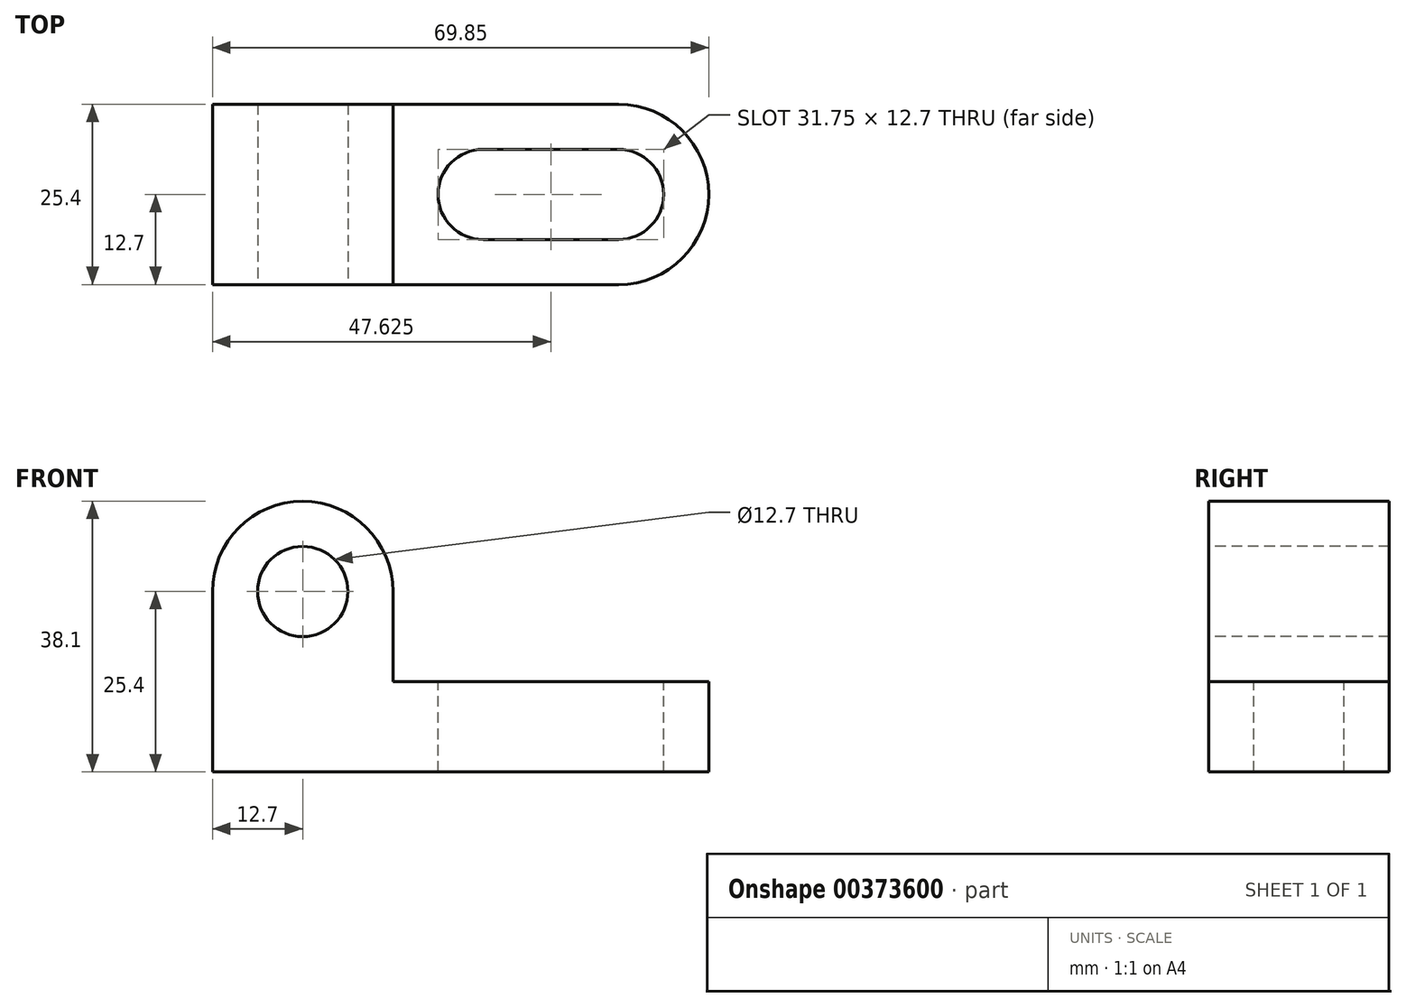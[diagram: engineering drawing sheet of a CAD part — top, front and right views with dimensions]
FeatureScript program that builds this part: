
annotation { "Feature Type Name" : "Feature", "Feature Type Description" : "" }
export const myFeature = defineFeature(function(context is Context, id is Id, definition is map)
    precondition{}
    {
        {
            var Q0;
            Q0=qCreatedBy(makeId("Front.planeOp"),FACE);
            var sketch = newSketch(context, id + "F0", { "sketchPlane" : qUnion([Q0])});
            skLineSegment(sketch, "E0", {"start": v(0, 0) * mm, "end": v(69.85, 0) * mm});
            skLineSegment(sketch, "E1", {"start": v(69.85, 0) * mm, "end": v(69.85, 12.7) * mm});
            skLineSegment(sketch, "E2", {"start": v(69.85, 12.7) * mm, "end": v(25.4, 12.7) * mm});
            skLineSegment(sketch, "E3", {"start": v(25.4, 12.7) * mm, "end": v(25.4, 38.1) * mm});
            skLineSegment(sketch, "E4", {"start": v(25.4, 38.1) * mm, "end": v(0, 38.1) * mm});
            skLineSegment(sketch, "E5", {"start": v(0, 38.1) * mm, "end": v(0, 0) * mm});
            skSolve(sketch);
        }
        {
            var Q0;
            Q0 = qSketchRegion(id + "F0", true);
            extrude(context, id + "F1", {"entities" : qUnion([Q0]), "depth" : 25.4 * mm});
        }
        {
            var Q0;
            Q0=makeQuery(id+"F1.opExtrude","CAP_FACE",FACE,{"disambiguationData":[OSD([sQuery(id+"F0.wireOp",EDGE,"E0"),sQuery(id+"F0.wireOp",EDGE,"E1"),sQuery(id+"F0.wireOp",EDGE,"E2"),sQuery(id+"F0.wireOp",EDGE,"E3"),sQuery(id+"F0.wireOp",EDGE,"E4"),sQuery(id+"F0.wireOp",EDGE,"E5")])],"isStart":false});
            var sketch = newSketch(context, id + "F2", { "sketchPlane" : qUnion([Q0])});
            skCircle(sketch, "E6", {"center": v(12.7, 25.4) * mm, "radius": 6.35 * mm});
            skPoint(sketch, "E6.centerSnap0", {"position": v(12.7, 38.1) * mm});
            skArc(sketch, "E7", {"start": v(25.4, 25.4) * mm, "mid": v(12.7, 38.1) * mm, "end": v(0, 25.4) * mm});
            skSolve(sketch);
        }
        {
            var Q0;
            {var subQ0=sQuery(id+"F2.wireOp",EDGE,"E7");var subQ1=makeQuery(id+"F1.opExtrude","CAP_EDGE",EDGE,{"disambiguationData":[OSD([sQuery(id+"F0.wireOp",EDGE,"E5")])],"isStart":false});var subQ2=makeQuery(id+"F2.imprint","INTERSECT",VERTEX,{"derivedFrom":[subQ1,subQ0]});Q0=makeQuery(id+"F2.imprint","IMPRINT",FACE,{"disambiguationData":[TD([[makeQuery(id+"F2.imprint","IMPRINT",EDGE,{"disambiguationData":[TD([[subQ2,1.0]])],"derivedFrom":subQ0}),-1.0]])]});}
            var Q1;
            {var subQ0=sQuery(id+"F2.wireOp",EDGE,"E7");var subQ1=makeQuery(id+"F1.opExtrude","CAP_EDGE",EDGE,{"disambiguationData":[OSD([sQuery(id+"F0.wireOp",EDGE,"E3")])],"isStart":false});var subQ2=makeQuery(id+"F2.imprint","INTERSECT",VERTEX,{"derivedFrom":[subQ1,subQ0]});Q1=makeQuery(id+"F2.imprint","IMPRINT",FACE,{"disambiguationData":[TD([[makeQuery(id+"F2.imprint","IMPRINT",EDGE,{"disambiguationData":[TD([[subQ2,-1.0]])],"derivedFrom":subQ0}),-1.0]])]});}
            var Q2;
            Q2=makeQuery(id+"F2.imprint","IMPRINT",FACE,{"disambiguationData":[TD([[makeQuery(id+"F2.imprint","IMPRINT",EDGE,{"derivedFrom":sQuery(id+"F2.wireOp",EDGE,"E6")}),1.0]])]});
            extrude(context, id + "F3", {"entities" : qUnion([Q0, Q1, Q2]), "operationType" : NewBodyOperationType.REMOVE, "oppositeDirection" : true, "depth" : 25.4 * mm});
        }
        {
            var Q0;
            Q0=makeQuery(id+"F1.opExtrude","SWEPT_FACE",FACE,{"disambiguationData":[OSD([sQuery(id+"F0.wireOp",EDGE,"E2")])]});
            var sketch = newSketch(context, id + "F4", { "sketchPlane" : qUnion([Q0])});
            skCircle(sketch, "E8", {"center": v(38.1, -12.7) * mm, "radius": 6.35 * mm});
            skPoint(sketch, "E8.centerSnap0", {"position": v(25.4, -12.7) * mm});
            skCircle(sketch, "E9", {"center": v(57.15, -12.7) * mm, "radius": 6.35 * mm});
            skLineSegment(sketch, "E10", {"start": v(38.1, -19.05) * mm, "end": v(57.15, -19.05) * mm});
            skLineSegment(sketch, "E11", {"start": v(38.1, -6.35) * mm, "end": v(57.15, -6.35) * mm});
            skArc(sketch, "E12", {"start": v(57.15, -25.4) * mm, "mid": v(69.85, -12.7) * mm, "end": v(57.15, 0) * mm});
            skSolve(sketch);
        }
        {
            var Q0;
            {var subQ0=sQuery(id+"F4.wireOp",EDGE,"E12");var subQ1=sQuery(id+"F0.wireOp",EDGE,"E2");var subQ2=makeQuery(id+"F1.opExtrude","CAP_EDGE",EDGE,{"disambiguationData":[OSD([subQ1])],"isStart":true});var subQ3=makeQuery(id+"F4.imprint","INTERSECT",VERTEX,{"derivedFrom":[subQ2,subQ0]});Q0=makeQuery(id+"F4.imprint","IMPRINT",FACE,{"disambiguationData":[TD([[makeQuery(id+"F4.imprint","IMPRINT",EDGE,{"disambiguationData":[TD([[subQ3,1.0]])],"derivedFrom":subQ0}),-1.0]])]});}
            var Q1;
            {var subQ0=sQuery(id+"F4.wireOp",EDGE,"E12");var subQ1=sQuery(id+"F0.wireOp",EDGE,"E2");var subQ2=makeQuery(id+"F1.opExtrude","CAP_EDGE",EDGE,{"disambiguationData":[OSD([subQ1])],"isStart":false});var subQ3=makeQuery(id+"F4.imprint","INTERSECT",VERTEX,{"derivedFrom":[subQ2,subQ0]});Q1=makeQuery(id+"F4.imprint","IMPRINT",FACE,{"disambiguationData":[TD([[makeQuery(id+"F4.imprint","IMPRINT",EDGE,{"disambiguationData":[TD([[subQ3,-1.0]])],"derivedFrom":subQ0}),-1.0]])]});}
            var Q2;
            {var subQ0=sQuery(id+"F4.wireOp",EDGE,"E8");var subQ3=makeQuery(id+"F4.imprint","INTERSECT",VERTEX,{"derivedFrom":[subQ0,sQuery(id+"F4.wireOp",EDGE,"E10")]});Q2=makeQuery(id+"F4.imprint","IMPRINT",FACE,{"disambiguationData":[TD([[makeQuery(id+"F4.imprint","IMPRINT",EDGE,{"disambiguationData":[TD([[subQ3,-1.0]])],"derivedFrom":subQ0}),1.0]])]});}
            var Q3;
            {var subQ0=sQuery(id+"F4.wireOp",EDGE,"E10");Q3=makeQuery(id+"F4.imprint","IMPRINT",FACE,{"disambiguationData":[TD([[makeQuery(id+"F4.imprint","IMPRINT",EDGE,{"derivedFrom":subQ0}),1.0]])]});}
            var Q4;
            {var subQ0=sQuery(id+"F4.wireOp",EDGE,"E9");var subQ1=makeQuery(id+"F4.imprint","INTERSECT",VERTEX,{"derivedFrom":[subQ0,sQuery(id+"F4.wireOp",EDGE,"E10")]});Q4=makeQuery(id+"F4.imprint","IMPRINT",FACE,{"disambiguationData":[TD([[makeQuery(id+"F4.imprint","IMPRINT",EDGE,{"disambiguationData":[TD([[subQ1,1.0]])],"derivedFrom":subQ0}),1.0]])]});}
            extrude(context, id + "F5", {"entities" : qUnion([Q0, Q1, Q2, Q3, Q4]), "operationType" : NewBodyOperationType.REMOVE, "oppositeDirection" : true, "depth" : 25.4 * mm});
        }
    });
